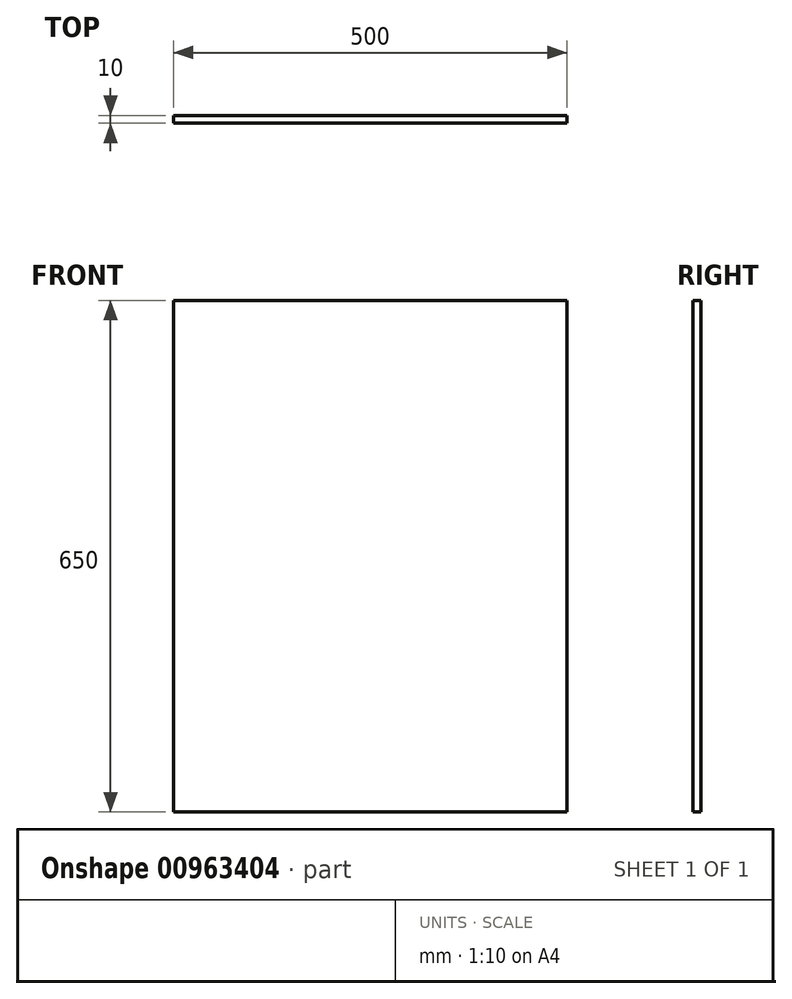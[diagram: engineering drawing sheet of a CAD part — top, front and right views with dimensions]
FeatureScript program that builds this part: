
annotation { "Feature Type Name" : "Feature", "Feature Type Description" : "" }
export const myFeature = defineFeature(function(context is Context, id is Id, definition is map)
    precondition{}
    {
        {
            var Q0;
            Q0=qCreatedBy(makeId("Front.planeOp"),FACE);
            var sketch = newSketch(context, id + "F0", { "sketchPlane" : qUnion([Q0])});
            skLineSegment(sketch, "E0.bottom", {"start": v(250, -325) * mm, "end": v(-250, -325) * mm});
            skLineSegment(sketch, "E0.top", {"start": v(250, 325) * mm, "end": v(-250, 325) * mm});
            skLineSegment(sketch, "E0.left", {"start": v(250, -325) * mm, "end": v(250, 325) * mm});
            skLineSegment(sketch, "E0.right", {"start": v(-250, -325) * mm, "end": v(-250, 325) * mm});
            skPoint(sketch, "E0.middle", {"position": v(0, 0) * mm});
            skSolve(sketch);
        }
        {
            var Q0;
            Q0 = qSketchRegion(id + "F0", true);
            extrude(context, id + "F1", {"entities" : qUnion([Q0]), "depth" : 10 * mm, "offsetDistance" : 25 * mm});
        }
    });
